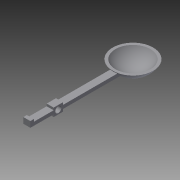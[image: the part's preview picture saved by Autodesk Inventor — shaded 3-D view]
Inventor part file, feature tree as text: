
AUTODESK INVENTOR PART (.ipt)
format: ipt  version: 2015 (Build 190159000, 159)  size: 145,920 bytes
history: native  units: in
note: dims shown in document units (in); Inventor stores cm internally (conversion verified against a paired STEP export)
features: sketch x7, extrude x5, revolve x1, plane x1, hole x1, projected_geometry x1
ambient origin geometry x8: Origin, YZ Plane, XZ Plane, XY Plane, X Axis, Y Axis, Z Axis, Center Point
bodies: Solid1 (feature_tree)
feature tree (16):
  revolve  "Revolution1"  [1 undecoded]
  plane  "Work Plane1"
  extrude  "Extrusion1"  Depth=0.25in
  extrude  "Extrusion2"  Depth=0.425in
  extrude  "Extrusion3"  Depth=0.075in
  sketch  "Sketch6"  dims[d14=0.075in d15=0.025in]
  extrude  "Extrusion4"  Depth=0.025in
  hole  "Hole1"  [1 undecoded]
  extrude  "Extrusion5"  Depth=0.05in
  sketch  "Sketch2"  dims[d4=1.0in d5=0.9in]
  sketch  "Sketch3"  dims[d8=180.0deg d9=0.25in]
  sketch  "Sketch4"  dims[d10=0.433in d11=0.425in]
  projected_geometry  "Projected Loop1"
  sketch  "Sketch5"  dims[d12=0.075in d13=0.075in]
  sketch  "Sketch7"  dims[d16=1.85in d17=0.069in d18=0.0in d19=0.0in d20=0.04in d21=0.0in]
  sketch  "Sketch8"  dims[d22=0.04in d23=0.0in d24=0.0375in d25=0.6in d26=0.6in d27=0.1in d28=0.1in d29=0.05in d30=0.125in d31=0.0in d32=0.0in d33=0.13in d34=0.75in d35=0.375in d36=0.25in d37=0.5635in d38=1.0in d39=0.8108in d40=0.075in d41=0.05in d42=0.0in]
note: 2 required parameter values undecoded (feature->parameter linkage not recoverable at this tier; creation-order binding heuristic only, values carry confidence <= 0.55)